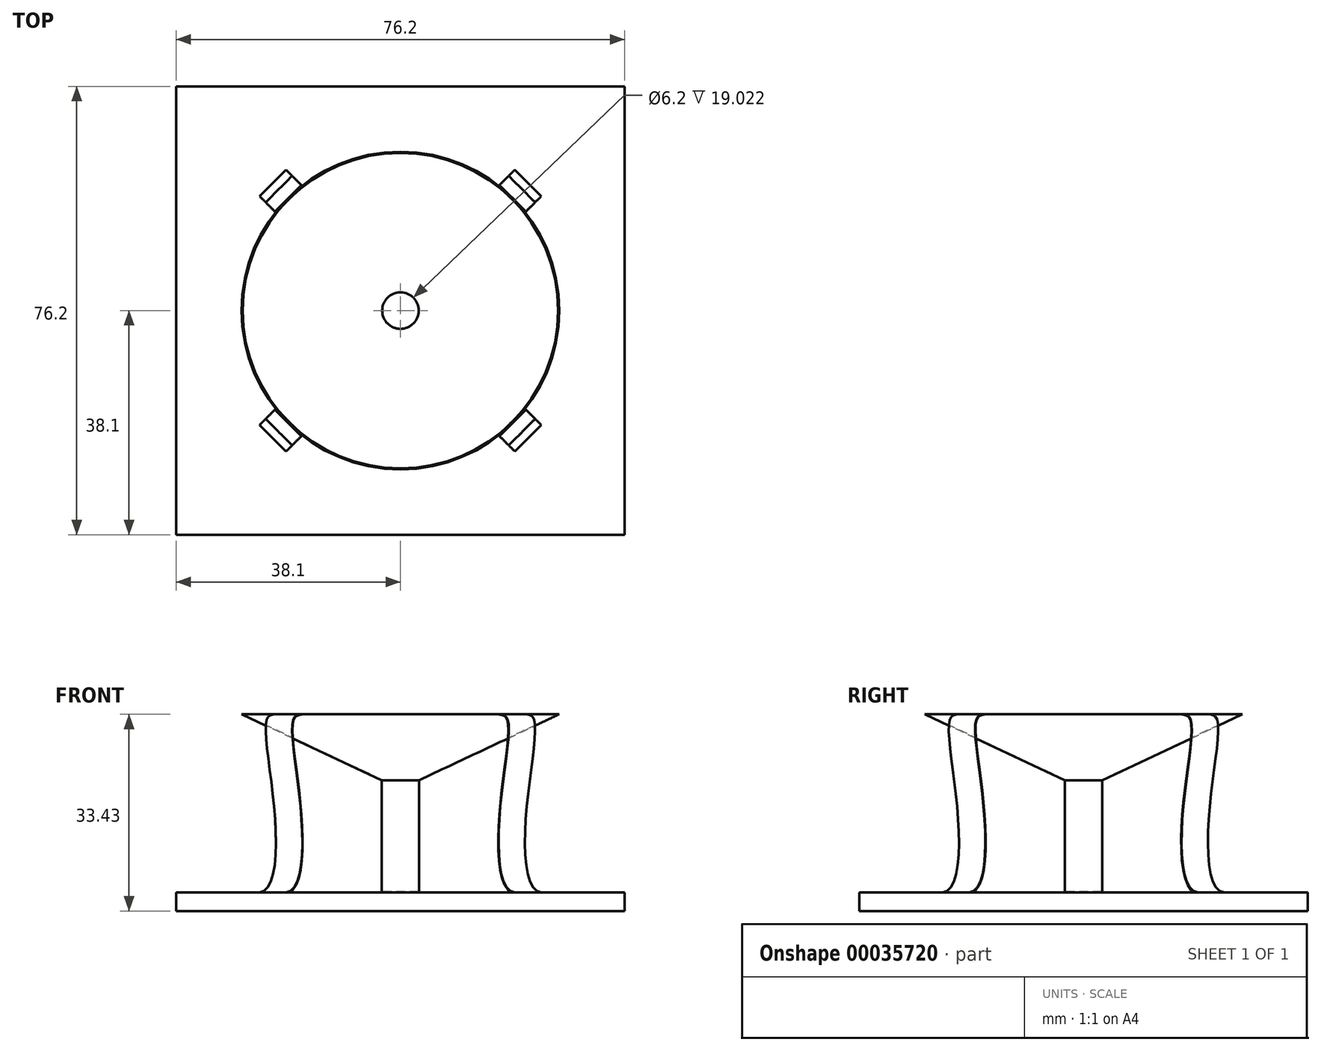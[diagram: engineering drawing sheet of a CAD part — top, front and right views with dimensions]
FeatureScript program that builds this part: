
annotation { "Feature Type Name" : "Feature", "Feature Type Description" : "" }
export const myFeature = defineFeature(function(context is Context, id is Id, definition is map)
    precondition{}
    {
        {
            var Q0;
            Q0=qCreatedBy(makeId("Top.planeOp"),FACE);
            var sketch = newSketch(context, id + "F0", { "sketchPlane" : qUnion([Q0])});
            skLineSegment(sketch, "E0.bottom", {"start": v(-38.1, 38.1) * mm, "end": v(38.1, 38.1) * mm});
            skLineSegment(sketch, "E0.top", {"start": v(-38.1, -38.1) * mm, "end": v(38.1, -38.1) * mm});
            skLineSegment(sketch, "E0.left", {"start": v(-38.1, 38.1) * mm, "end": v(-38.1, -38.1) * mm});
            skLineSegment(sketch, "E0.right", {"start": v(38.1, 38.1) * mm, "end": v(38.1, -38.1) * mm});
            skSolve(sketch);
        }
        {
            var Q0;
            Q0=makeQuery(id+"F0.imprint","IMPRINT",FACE,{"disambiguationData":[TD([[makeQuery(id+"F0.imprint","IMPRINT",EDGE,{"derivedFrom":sQuery(id+"F0.wireOp",EDGE,"E0.bottom")}),-1.0]])]});
            extrude(context, id + "F1", {"entities" : qUnion([Q0]), "depth" : 3.17 * mm});
        }
        {
            var Q0;
            Q0=makeQuery(id+"F1.opExtrude","CAP_FACE",FACE,{"disambiguationData":[OSD([sQuery(id+"F0.wireOp",EDGE,"E0.bottom"),sQuery(id+"F0.wireOp",EDGE,"E0.top"),sQuery(id+"F0.wireOp",EDGE,"E0.left"),sQuery(id+"F0.wireOp",EDGE,"E0.right")])],"isStart":false});
            var sketch = newSketch(context, id + "F2", { "sketchPlane" : qUnion([Q0])});
            skCircle(sketch, "E1", {"center": v(0, 0) * mm, "radius": 3.18 * mm});
            skSolve(sketch);
        }
        {
            var Q0;
            Q0 = qSketchRegion(id + "F2", true);
            extrude(context, id + "F3", {"entities" : qUnion([Q0]), "depth" : 19.05 * mm});
        }
        {
            var Q0;
            Q0=qCreatedBy(makeId("Front.planeOp"),FACE);
            var sketch = newSketch(context, id + "F4", { "sketchPlane" : qUnion([Q0])});
            skLineSegment(sketch, "E2", {"start": v(0, 20.73) * mm, "end": v(26.99, 33.43) * mm});
            skLineSegment(sketch, "E3", {"start": v(26.99, 33.43) * mm, "end": v(0, 33.43) * mm});
            skLineSegment(sketch, "E4", {"start": v(0, 33.43) * mm, "end": v(0, 20.73) * mm});
            skLineSegment(sketch, "E5", {"start": v(3.18, 22.23) * mm, "end": v(3.18, 3.18) * mm});
            skSolve(sketch);
        }
        {
            var Q0;
            {var subQ1=sQuery(id+"F4.wireOp",EDGE,"E3");Q0=makeQuery(id+"F4.imprint","IMPRINT",FACE,{"disambiguationData":[TD([[makeQuery(id+"F4.imprint","IMPRINT",EDGE,{"derivedFrom":subQ1}),1.0]])]});}
            var Q1;
            Q1=sQuery(id+"F4.wireOp",EDGE,"E4");
            revolve(context, id + "F5", {"operationType" : NewBodyOperationType.ADD, "entities" : qUnion([Q0]), "axis" : qUnion([Q1]), "revolveType" : RevolveType.FULL});
        }
        {
            var Q0;
            Q0=makeQuery(id+"F5.opRevolve","SWEPT_FACE",FACE,{"disambiguationData":[OSD([sQuery(id+"F4.wireOp",EDGE,"E3")])]});
            shell(context, id + "F6", {"entities" : qUnion([Q0]), "thickness" : 0.08 * mm});
        }
        {
            var Q0;
            Q0=makeQuery(id+"F1.opExtrude","CAP_VERTEX",VERTEX,{"disambiguationData":[OSD([sQuery(id+"F0.wireOp",EDGE,"E0.top"),sQuery(id+"F0.wireOp",EDGE,"E0.right")])],"isStart":true});
            var Q1;
            Q1=makeQuery(id+"F1.opExtrude","CAP_VERTEX",VERTEX,{"disambiguationData":[OSD([sQuery(id+"F0.wireOp",EDGE,"E0.top"),sQuery(id+"F0.wireOp",EDGE,"E0.right")])],"isStart":false});
            var Q2;
            Q2=makeQuery(id+"F1.opExtrude","CAP_VERTEX",VERTEX,{"disambiguationData":[OSD([sQuery(id+"F0.wireOp",EDGE,"E0.bottom"),sQuery(id+"F0.wireOp",EDGE,"E0.left")])],"isStart":true});
            cPlane(context, id + "F7", {"entities" : qUnion([Q0, Q1, Q2]), "cplaneType" : CPlaneType.THREE_POINT, "offset" : 152.4 * mm, "width" : 152.4 * mm, "height" : 152.4 * mm});
        }
        {
            var Q0;
            Q0=qCreatedBy(id+"F7.planeOp",FACE);
            var sketch = newSketch(context, id + "F8", { "sketchPlane" : qUnion([Q0])});
            skLineSegment(sketch, "E6.0", {"start": v(-53.88, 3.18) * mm, "end": v(-53.88, 0) * mm});
            skLineSegment(sketch, "E7.0", {"start": v(0, 3.18) * mm, "end": v(-53.88, 3.18) * mm, "construction": true});
            skLineSegment(sketch, "E8.0", {"start": v(-26.99, 33.43) * mm, "end": v(26.99, 33.43) * mm, "construction": true});
            skFitSpline(sketch, "E9", {"points": [v(-26.99, 33.43) * mm, v(-28.8, 32.79) * mm, v(-26.99, 16.07) * mm, v(-30.68, 3.18) * mm], "startDerivative": vector(-9.05, -1.82) * mm, "endDerivative": vector(-28, 0) * mm});
            skSolve(sketch);
        }
        {
            var Q0;
            Q0=sQuery(id+"F8.wireOp",VERTEX,"E9.0.internal");
            var Q1;
            Q1=sQuery(id+"F8.wireOp",EDGE,"E7.0");
            cPlane(context, id + "F9", {"entities" : qUnion([Q0, Q1]), "cplaneType" : CPlaneType.CURVE_POINT, "offset" : 152.4 * mm, "width" : 152.4 * mm, "height" : 152.4 * mm});
        }
        {
            var Q0;
            Q0=qCreatedBy(id+"F9.planeOp",FACE);
            var sketch = newSketch(context, id + "F10", { "sketchPlane" : qUnion([Q0])});
            skPoint(sketch, "E10.0", {"position": v(0, 33.43) * mm});
            skLineSegment(sketch, "E11.bottom", {"start": v(-3.18, 33.43) * mm, "end": v(3.18, 33.43) * mm});
            skLineSegment(sketch, "E11.top", {"start": v(-3.17, 33.35) * mm, "end": v(3.18, 33.35) * mm});
            skLineSegment(sketch, "E11.left", {"start": v(-3.18, 33.43) * mm, "end": v(-3.18, 33.35) * mm});
            skLineSegment(sketch, "E11.right", {"start": v(3.18, 33.43) * mm, "end": v(3.18, 33.35) * mm});
            skSolve(sketch);
        }
        {
            var Q0;
            Q0 = qSketchRegion(id + "F10", true);
            var Q1;
            Q1=sQuery(id+"F8.wireOp",EDGE,"E9");
            sweep(context, id + "F11", {"profiles" : qUnion([Q0]), "path" : qUnion([Q1])});
        }
        {
            var Q0;
            Q0=makeQuery(id+"F11.opSweep","SWEPT_BODY",BODY,{"disambiguationData":[OSD([sQuery(id+"F8.wireOp",EDGE,"E9"),sQuery(id+"F10.wireOp",EDGE,"E11.bottom"),sQuery(id+"F10.wireOp",EDGE,"E11.top"),sQuery(id+"F10.wireOp",EDGE,"E11.left"),sQuery(id+"F10.wireOp",EDGE,"E11.right")])]});
            var Q1;
            Q1=makeQuery(id+"F3.opExtrude","SWEPT_FACE",FACE,{"disambiguationData":[OSD([sQuery(id+"F2.wireOp",EDGE,"E1")])]});
            circularPattern(context, id + "F12", {"entities" : qUnion([Q0]), "axis" : qUnion([Q1]), "angle" : 90 * degree, "instanceCount" : 4});
        }
    });
